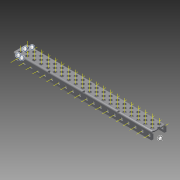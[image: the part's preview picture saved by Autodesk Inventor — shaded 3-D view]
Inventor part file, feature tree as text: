
AUTODESK INVENTOR PART (.ipt)
format: ipt  version: 2015 SP1 (Build 190203100, 203)  size: 2,144,256 bytes
history: native  units: in
note: dims shown in document units (in); Inventor stores cm internally (conversion verified against a paired STEP export)
features: other x106, pattern_linear x3, sheet_metal_op x1, extrude x1, imported_body x1, sketch x1
ambient origin geometry x8: Origin, YZ Plane, XZ Plane, XY Plane, X Axis, Y Axis, Z Axis, Center Point
bodies: Body1 (feature_tree)
feature tree (113):
  sheet_metal_op  "Fold1"
  other  "C-Channel"
  extrude  "length cut"  Depth=0.5in
  other  "top axis"
  other  "inner axis"
  other  "front axis"
  other  "back axis"
  pattern_linear  "top axes"  Spacing1=0.5in  [1 undecoded]
  pattern_linear  "inner axes"  Spacing1=0.5in  [1 undecoded]
  pattern_linear  "horiz axes"  Spacing1=-10.0in  [1 undecoded]
  other  "right plane"
  imported_body  "Base1"
  sketch  "Sketch1"  dims[d1=0.0in d4=0.5in d5=0.7874in d7=0.5in d10=0.5in d13=0.5in d14=-10.0in d15=0.0in d16=0.0in d17=0.0in d18=0.0in d19=0.0in]
  other  "Work Point1"
  other  "Work Point2"
  other  "Work Point3"
  other  "Work Point4"
  other  "Work Axis5"
  other  "Work Axis6"
  other  "Work Axis7"
  other  "Work Axis8"
  other  "Work Axis11"
  other  "Work Axis12"
  other  "Work Axis13"
  other  "Work Axis14"
  other  "Work Axis15"
  other  "Work Axis18"
  other  "Work Axis19"
  other  "Work Axis20"
  other  "Work Axis23"
  other  "Work Axis24"
  other  "Work Axis25"
  other  "Work Axis26"
  other  "Work Axis30"
  other  "Work Axis31"
  other  "Work Axis32"
  other  "Work Axis33"
  other  "left plane"
  other  "Work Axis37"
  other  "Work Axis38"
  other  "Work Axis39"
  other  "Work Axis40"
  other  "Work Axis41"
  other  "Work Axis42"
  other  "Work Axis43"
  other  "Work Axis44"
  other  "Work Axis45"
  other  "Work Axis46"
  other  "Work Axis57"
  other  "Work Axis58"
  other  "Work Axis59"
  other  "Work Axis60"
  other  "Work Axis61"
  other  "Work Axis62"
  other  "Work Axis63"
  other  "Work Axis64"
  other  "Work Axis65"
  other  "Work Axis66"
  other  "Work Axis77"
  other  "Work Axis78"
  other  "Work Axis79"
  other  "Work Axis80"
  other  "Work Axis81"
  other  "Work Axis82"
  other  "Work Axis83"
  other  "Work Axis84"
  other  "Work Axis85"
  other  "Work Axis86"
  other  "Work Axis97"
  other  "Work Axis98"
  other  "Work Axis99"
  other  "Work Axis100"
  other  "Work Axis101"
  other  "Work Axis102"
  other  "Work Axis103"
  other  "Work Axis104"
  other  "Work Axis105"
  other  "Work Axis106"
  other  "Work Axis117"
  other  "Work Axis118"
  other  "Work Axis119"
  other  "Work Axis120"
  other  "Work Axis121"
  other  "Work Axis122"
  other  "Work Axis123"
  other  "Work Axis124"
  other  "Work Axis125"
  other  "Work Axis126"
  other  "Work Axis137"
  other  "Work Axis138"
  other  "Work Axis139"
  other  "Work Axis140"
  other  "Work Axis141"
  other  "Work Axis142"
  other  "Work Axis143"
  other  "Work Axis144"
  other  "Work Axis145"
  other  "Work Axis146"
  other  "Work Axis147"
  other  "Work Axis148"
  other  "Work Axis149"
  other  "Work Axis150"
  other  "Work Axis151"
  other  "Work Axis152"
  other  "Work Axis153"
  other  "Work Axis154"
  other  "Work Axis155"
  other  "Work Axis156"
  other  "Work Axis157"
  other  "Work Axis158"
  other  "Work Axis159"
  other  "Work Axis160"
  other  "Work Axis161"
note: 3 required parameter values undecoded (feature->parameter linkage not recoverable at this tier; creation-order binding heuristic only, values carry confidence <= 0.55)
